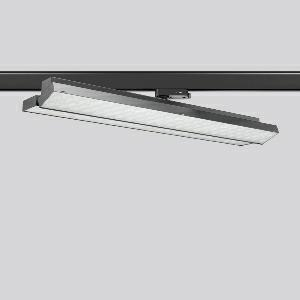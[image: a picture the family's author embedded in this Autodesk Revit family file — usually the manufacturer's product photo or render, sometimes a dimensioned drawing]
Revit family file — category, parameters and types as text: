
# Revit family: tx-move_742161_003_3_4fe5
name_source: partatom
category: Lighting Fixtures
units: mm (PartAtom-declared; Revit-internal decimal feet)

## family parameters
Cut with Voids When Loaded = No
Host = Face
Light Source = No
Part Type = Normal
Room Calculation Point = No
Round Connector Dimension = Use Diameter
Shared = No

## types (1)
- MultiLumen 1 (1 x LED Modul 835, 3025 lm, 3500)
    Apparent Load = 41 VA
    CIE Flux Codes = 88 96 99 100 100
    Color Rendering = 80
    Color Temperature = 3500
    Default Elevation = 1800 mm
    Description = Series: TX-MOVE
Multifunctional surface-mounted spotlight for area lighting. Very flat design. Housing: sheet steel, powder-coated. Rotation range: 356°. Swivel range: 90°. Consistent alignment possible with visible tilt scale. High-efficiency LED units with optimum light control thanks to clear plastic (PC) lens optics. Spezielle Mikrostrukturen reduzieren Gelbsaum. Symmetrical light distribution. With multi adaptor for 3-circuit tracks 230 V. Suitable for Track on ceiling. MultiLumen: Luminous flux adjustable in 3 steps. Factory setting is the highest luminous flux. Environmentally friendly and resource-saving due to replaceable and recyclable components. 
Colour: deep black, matt (RAL 9005)
Length: 570 mm
Width: 119 mm
Height: 92 mm
Lamp: LED
Socket: without socket
Colour temperature: 3500K
Colour rendering index (CRI): 80
System power: 41 W
Rated luminous flux: 6050 lm
Luminous efficiency: 148 lm/W
System power 2: 57 W
Rated luminous flux 2: 8200 lm
Luminous efficiency 2: 144 lm/W
System power 3: 73 W
Rated luminous flux 3: 10000 lm
Luminous efficiency 3: 137 lm/W
Control gear: Regulated power supply
Protection class: I
Type of protection: IP 20
    Height = 75 mm
    Lamp = 1 x LED Modul 835
    Lamp Light Flux = 3025 lm
    Lamp count = 1
    Length = 569 mm
    Lifetime = 50000 h
    Luminous efficacy = 148 lm/W
    Manufacturer = RZB
    ModVariant = No
    Model = 742161.003.3
    Mounting Place = Ceiling
    Mounting Type = Rail mounted
    Number of Poles = 1
    OnlyDefault = Yes
    Power Factor = 1
    Product Name = TX-MOVE
    Product group = Track mounted projectors
    ProductGroupID = 301
    Protection Class = Protection class I
    Protection Degree = IP 20
    RLX_Detail_Level = 1
    RLX_Emergency_Light_Flux = 0 lm
    RLX_Emergency_Type = 0
    RLX_Emergency_Type_DB = No
    RlxData = <blob elided: 36949 chars, md5=3eacdcaa>
    Socket = socket
    Standby Power = 0 W
    System Light Flux = 6050 lm
    System Power = 41 W
    Type Comments = MultiLumen 1
    Type Image = 742162.003.jpg
    URL = http://relux.com
    VarID = multilumen_1
    Voltage = 230 V
    Voltage Range = 220-240 V
    Weight = 0.00 kg
    Width = 119 mm

## geometry (parser evidence)
native form markers: Blend x4, Sweep x13
no freeform markers — native parametric forms only
